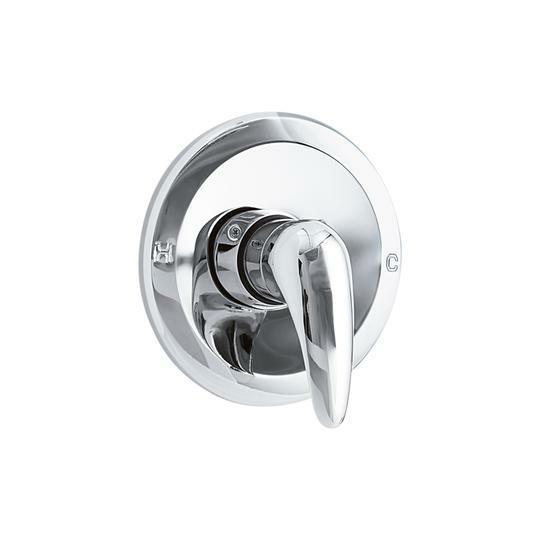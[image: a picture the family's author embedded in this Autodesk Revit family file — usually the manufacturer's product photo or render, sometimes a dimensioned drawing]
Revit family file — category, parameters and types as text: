
# Revit family: 01-2201-11SR DUCHA MONOMANDO SST SIN REGADERA TIFFANY
name_source: partatom
category: Aparatos sanitarios
revit_build: Autodesk Revit 2018 (Build: 20170223_1515(x64)
units: mm (PartAtom-declared; Revit-internal decimal feet)

## family parameters
Anfitrión = Cara
Compartido = No
Corte con vacíos al cargar = No
Cota de conector redondo = Diámetro de uso
Número OmniClass = 23.31.11.00
Punto de cálculo de habitación = No
Tipo de pieza = Normal

## types (1)
- 01-2201-11SR
    Conexión AC = Sí
    Conexión AF = Sí
    Conexión de residuos = No
    Conexión de ventilación = No
    Descripción = Griferia Monomando Ducha
    Diametro = 180 mm
    Elevación por defecto = 0 mm  [stored 0 ft]
    Fabricante = Gricol
    Finish = Cromo Gricol
    Imagen de tipo = <Ninguno>
    Link Ficha Tecnica = https://infotecnica.gricol.com
    Modelo = 01-2201-11SR
    Product Name = DUCHA MONOMANDO SST SIN REGADERA TIFFANY
    Profundidad = 72 mm  [stored 0.23622 ft]
    URL = https://www.gricol.com

note: [stored X ft] marks values corroborated as IEEE doubles in the binary element streams (Revit-internal decimal feet)

## geometry (parser evidence)
native form markers: Blend x2, Sweep x25
no freeform markers — native parametric forms only
